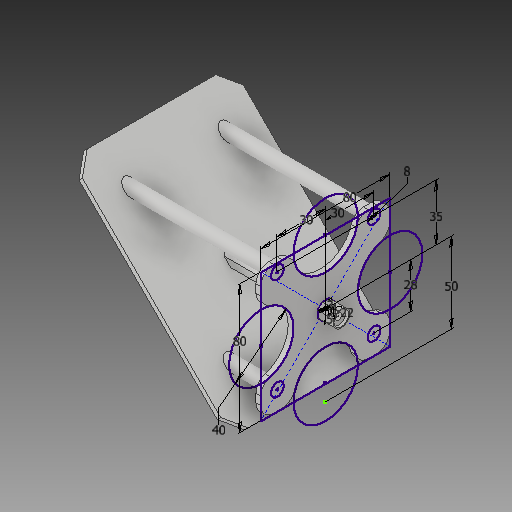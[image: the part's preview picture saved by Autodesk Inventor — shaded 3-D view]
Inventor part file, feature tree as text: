
AUTODESK INVENTOR PART (.ipt)
format: ipt  version: 2017 (Build 210142000, 142)  size: 251,904 bytes
history: native  units: mm
features: extrude x8, sketch x2, chamfer x1, fillet x1
ambient origin geometry x8: Origin, YZ Plane, XZ Plane, XY Plane, X Axis, Y Axis, Z Axis, Center Point
bodies: Solid1 (feature_tree)
feature tree (12):
  extrude  "Extrusion1"  Depth=10.0mm TaperAngle=45.0deg
  chamfer  "Chamfer1"  Distance=4.0mm
  sketch  "Sketch2"  dims[d8=50.0mm d10=4.0mm d11=5.0mm d12=100.0mm d13=0.0mm d14=3.0mm d15=30.0mm d16=30.0mm d17=35.0mm d18=28.0mm d19=8.0mm d20=3.0mm d21=0.0mm d22=5.0mm d23=0.0mm d24=10.0mm d25=3.0mm d26=45.0deg d27=100.0mm d28=80.0mm d29=80.0mm d32=5.0mm d33=0.0mm d34=8.0mm d35=9.22mm d38=40.0mm d39=10.0mm d40=0.0mm d41=8.25mm d42=0.0mm d43=6.22mm d44=0.0mm]
  extrude  "Extrusion2"  Depth=6.22mm
  extrude  "Extrusion3"  Depth=100.0mm TaperAngle=0.0deg
  extrude  "Extrusion4"  Depth=3.0mm
  extrude  "Extrusion5"  Depth=6.22mm
  fillet  "Fillet2"  Radius=30.0mm
  extrude  "Extrusion7"  Depth=35.0mm
  extrude  "Extrusion8"  Depth=6.22mm
  extrude  "Extrusion9"  Depth=8.0mm
  sketch  "Sketch1"  dims[d3=100.0mm d4=0.0mm d5=10.0mm d6=2.0mm d7=45.0deg]
